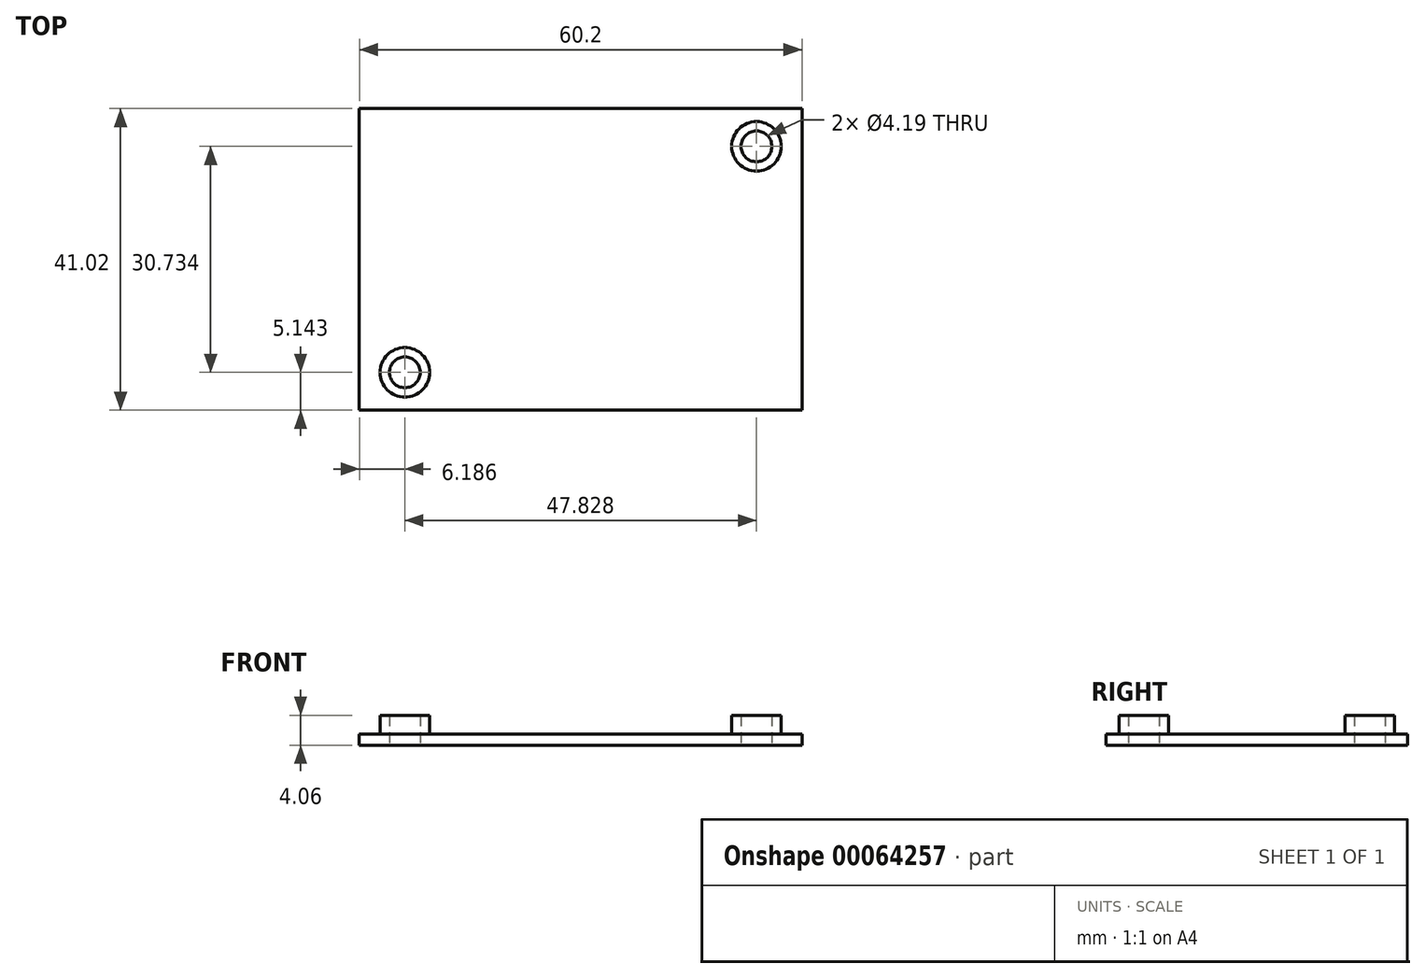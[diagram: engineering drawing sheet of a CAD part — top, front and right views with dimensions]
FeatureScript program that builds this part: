
annotation { "Feature Type Name" : "Feature", "Feature Type Description" : "" }
export const myFeature = defineFeature(function(context is Context, id is Id, definition is map)
    precondition{}
    {
        {
            var Q0;
            Q0=qCreatedBy(makeId("Top.planeOp"),FACE);
            var sketch = newSketch(context, id + "F0", { "sketchPlane" : qUnion([Q0])});
            skLineSegment(sketch, "E0.bottom", {"start": v(19.24, -13.08) * mm, "end": v(-19.24, -13.08) * mm});
            skLineSegment(sketch, "E0.top", {"start": v(19.24, 13.08) * mm, "end": v(-19.24, 13.08) * mm});
            skLineSegment(sketch, "E0.left", {"start": v(19.24, -13.08) * mm, "end": v(19.24, 13.08) * mm});
            skLineSegment(sketch, "E0.right", {"start": v(-19.24, -13.08) * mm, "end": v(-19.24, 13.08) * mm});
            skPoint(sketch, "E0.middle", {"position": v(0, 0) * mm});
            skSolve(sketch);
        }
        {
            var Q0;
            Q0=qCreatedBy(makeId("Top.planeOp"),FACE);
            var sketch = newSketch(context, id + "F1", { "sketchPlane" : qUnion([Q0])});
            skLineSegment(sketch, "E1.bottom", {"start": v(21.53, -15.37) * mm, "end": v(-21.53, -15.37) * mm});
            skLineSegment(sketch, "E1.top", {"start": v(21.53, 15.37) * mm, "end": v(-21.53, 15.37) * mm});
            skLineSegment(sketch, "E1.left", {"start": v(21.53, -15.37) * mm, "end": v(21.53, 15.37) * mm});
            skLineSegment(sketch, "E1.right", {"start": v(-21.53, -15.37) * mm, "end": v(-21.53, 15.37) * mm});
            skPoint(sketch, "E1.middle", {"position": v(0, 0) * mm});
            skSolve(sketch);
        }
        {
            var Q0;
            Q0=qCreatedBy(makeId("Top.planeOp"),FACE);
            var sketch = newSketch(context, id + "F2", { "sketchPlane" : qUnion([Q0])});
            skCircle(sketch, "E2.cCircle", {"center": v(-24.56, 15.37) * mm, "radius": 2.6 * mm, "construction": true});
            skLineSegment(sketch, "E2.0", {"start": v(-23.06, 12.76) * mm, "end": v(-26.06, 12.76) * mm});
            skLineSegment(sketch, "E2.1", {"start": v(-26.06, 12.76) * mm, "end": v(-27.56, 15.37) * mm});
            skLineSegment(sketch, "E2.2", {"start": v(-27.56, 15.37) * mm, "end": v(-26.06, 17.97) * mm});
            skLineSegment(sketch, "E2.3", {"start": v(-26.06, 17.97) * mm, "end": v(-23.06, 17.97) * mm});
            skLineSegment(sketch, "E2.4", {"start": v(-23.06, 17.97) * mm, "end": v(-21.55, 15.37) * mm});
            skLineSegment(sketch, "E2.5", {"start": v(-21.55, 15.37) * mm, "end": v(-23.06, 12.76) * mm});
            skPoint(sketch, "E2.0.midPoint", {"position": v(-24.56, 12.76) * mm});
            skSolve(sketch);
        }
        {
            var Q0;
            Q0=makeQuery(id+"F1.imprint","IMPRINT",FACE,{"disambiguationData":[TD([[makeQuery(id+"F1.imprint","IMPRINT",EDGE,{"derivedFrom":sQuery(id+"F1.wireOp",EDGE,"E1.bottom")}),-1.0]])]});
            var sketch = newSketch(context, id + "F3", { "sketchPlane" : qUnion([Q0])});
            skCircle(sketch, "E3", {"center": v(-24.56, 15.37) * mm, "radius": 1.46 * mm});
            skSolve(sketch);
        }
        {
            var Q0;
            Q0=makeQuery(id+"F1.imprint","IMPRINT",FACE,{"disambiguationData":[TD([[makeQuery(id+"F1.imprint","IMPRINT",EDGE,{"derivedFrom":sQuery(id+"F1.wireOp",EDGE,"E1.bottom")}),-1.0]])]});
            var sketch = newSketch(context, id + "F4", { "sketchPlane" : qUnion([Q0])});
            skCircle(sketch, "E4.cCircle", {"center": v(24.56, -15.37) * mm, "radius": 2.6 * mm, "construction": true});
            skLineSegment(sketch, "E4.0", {"start": v(26.06, -17.97) * mm, "end": v(23.06, -17.97) * mm});
            skLineSegment(sketch, "E4.1", {"start": v(23.06, -17.97) * mm, "end": v(21.55, -15.37) * mm});
            skLineSegment(sketch, "E4.2", {"start": v(21.55, -15.37) * mm, "end": v(23.06, -12.76) * mm});
            skLineSegment(sketch, "E4.3", {"start": v(23.06, -12.76) * mm, "end": v(26.06, -12.76) * mm});
            skLineSegment(sketch, "E4.4", {"start": v(26.06, -12.76) * mm, "end": v(27.56, -15.37) * mm});
            skLineSegment(sketch, "E4.5", {"start": v(27.56, -15.37) * mm, "end": v(26.06, -17.97) * mm});
            skPoint(sketch, "E4.0.midPoint", {"position": v(24.56, -17.97) * mm});
            skSolve(sketch);
        }
        {
            var Q0;
            Q0=makeQuery(id+"F1.imprint","IMPRINT",FACE,{"disambiguationData":[TD([[makeQuery(id+"F1.imprint","IMPRINT",EDGE,{"derivedFrom":sQuery(id+"F1.wireOp",EDGE,"E1.bottom")}),-1.0]])]});
            var sketch = newSketch(context, id + "F5", { "sketchPlane" : qUnion([Q0])});
            skCircle(sketch, "E5", {"center": v(24.56, -15.37) * mm, "radius": 1.46 * mm});
            skSolve(sketch);
        }
        {
            var Q0;
            Q0=makeQuery(id+"F1.imprint","IMPRINT",FACE,{"disambiguationData":[TD([[makeQuery(id+"F1.imprint","IMPRINT",EDGE,{"derivedFrom":sQuery(id+"F1.wireOp",EDGE,"E1.bottom")}),-1.0]])]});
            var sketch = newSketch(context, id + "F6", { "sketchPlane" : qUnion([Q0])});
            skCircle(sketch, "E6", {"center": v(-23.91, -15.37) * mm, "radius": 2.1 * mm});
            skLineSegment(sketch, "E7", {"start": v(-23.91, -15.37) * mm, "end": v(-21.53, -15.37) * mm, "construction": true});
            skCircle(sketch, "E8", {"center": v(-23.91, -15.37) * mm, "radius": 3.37 * mm});
            skSolve(sketch);
        }
        {
            var Q0;
            Q0=makeQuery(id+"F1.imprint","IMPRINT",FACE,{"disambiguationData":[TD([[makeQuery(id+"F1.imprint","IMPRINT",EDGE,{"derivedFrom":sQuery(id+"F1.wireOp",EDGE,"E1.bottom")}),-1.0]])]});
            var sketch = newSketch(context, id + "F7", { "sketchPlane" : qUnion([Q0])});
            skCircle(sketch, "E9", {"center": v(23.91, 15.37) * mm, "radius": 2.1 * mm});
            skLineSegment(sketch, "E10", {"start": v(23.91, 15.37) * mm, "end": v(21.53, 15.37) * mm, "construction": true});
            skLineSegment(sketch, "E11", {"start": v(-23.91, -15.37) * mm, "end": v(23.91, -15.37) * mm, "construction": true});
            skLineSegment(sketch, "E12", {"start": v(23.91, 15.37) * mm, "end": v(23.91, -15.37) * mm, "construction": true});
            skCircle(sketch, "E13", {"center": v(23.91, 15.37) * mm, "radius": 3.37 * mm});
            skSolve(sketch);
        }
        {
            var Q0;
            Q0=qCreatedBy(makeId("Top.planeOp"),FACE);
            var sketch = newSketch(context, id + "F8", { "sketchPlane" : qUnion([Q0])});
            skLineSegment(sketch, "E14.bottom", {"start": v(30.1, -20.51) * mm, "end": v(-30.1, -20.51) * mm});
            skLineSegment(sketch, "E14.top", {"start": v(30.1, 20.51) * mm, "end": v(-30.1, 20.51) * mm});
            skLineSegment(sketch, "E14.left", {"start": v(30.1, -20.51) * mm, "end": v(30.1, 20.51) * mm});
            skLineSegment(sketch, "E14.right", {"start": v(-30.1, -20.51) * mm, "end": v(-30.1, 20.51) * mm});
            skPoint(sketch, "E14.middle", {"position": v(0, 0) * mm});
            skSolve(sketch);
        }
        {
            var Q0;
            Q0=qSketchRegion(id+"F8",true);
            extrude(context, id + "F9", {"entities" : qUnion([Q0]), "depth" : 1.52 * mm, "hasOffset" : true, "offsetDistance" : 2.3 * mm});
        }
        {
            var Q0;
            Q0=qSketchRegion(id+"F6",true);
            var Q1;
            Q1=qSketchRegion(id+"F7",true);
            extrude(context, id + "F10", {"entities" : qUnion([Q0, Q1]), "operationType" : NewBodyOperationType.ADD, "depth" : 4.06 * mm, "offsetDistance" : 25.4 * mm});
        }
        {
            var Q0;
            Q0=makeQuery(id+"F10.boolean.opBoolean","SPLIT",FACE,{"disambiguationData":[TD([makeQuery(id+"F10.opExtrude","SWEPT_FACE",FACE,{"disambiguationData":[OSD([sQuery(id+"F6.wireOp",EDGE,"E6")])]})])],"derivedFrom":makeQuery(id+"F9.opExtrude","CAP_FACE",FACE,{"disambiguationData":[OSD([sQuery(id+"F8.wireOp",EDGE,"E14.bottom"),sQuery(id+"F8.wireOp",EDGE,"E14.top"),sQuery(id+"F8.wireOp",EDGE,"E14.left"),sQuery(id+"F8.wireOp",EDGE,"E14.right")])],"isStart":false})});
            var Q1;
            Q1=makeQuery(id+"F10.boolean.opBoolean","SPLIT",FACE,{"disambiguationData":[TD([makeQuery(id+"F10.opExtrude","SWEPT_FACE",FACE,{"disambiguationData":[OSD([sQuery(id+"F7.wireOp",EDGE,"E9")])]})])],"derivedFrom":makeQuery(id+"F9.opExtrude","CAP_FACE",FACE,{"disambiguationData":[OSD([sQuery(id+"F8.wireOp",EDGE,"E14.bottom"),sQuery(id+"F8.wireOp",EDGE,"E14.top"),sQuery(id+"F8.wireOp",EDGE,"E14.left"),sQuery(id+"F8.wireOp",EDGE,"E14.right")])],"isStart":false})});
            extrude(context, id + "F11", {"entities" : qUnion([Q0, Q1]), "operationType" : NewBodyOperationType.REMOVE, "oppositeDirection" : true, "depth" : 25.4 * mm, "offsetDistance" : 25.4 * mm});
        }
    });
